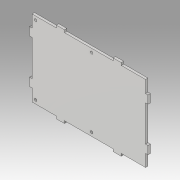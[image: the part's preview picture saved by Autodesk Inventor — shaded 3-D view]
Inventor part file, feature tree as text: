
AUTODESK INVENTOR PART (.ipt)
format: ipt  version: 2019.3 (Build 233278000, 278)  size: 137,216 bytes
history: native  units: mm
features: extrude x1, sketch x1
ambient origin geometry x8: Origin, YZ Plane, XZ Plane, XY Plane, X Axis, Y Axis, Z Axis, Center Point
bodies: Solid1 (feature_tree)
feature tree (2):
  extrude  "Extrusion1"  Depth=3.0mm
  sketch  "Sketch1"  dims[d0=3.1mm d1=85.0mm d2=69.0mm d3=94.0mm d4=4.5mm d5=4.5mm d6=4.5mm d7=140.0mm d8=3.0mm d9=10.0mm d10=15.0mm d11=15.0mm d12=30.0mm d13=30.0mm d14=3.0mm d15=0.0mm]
